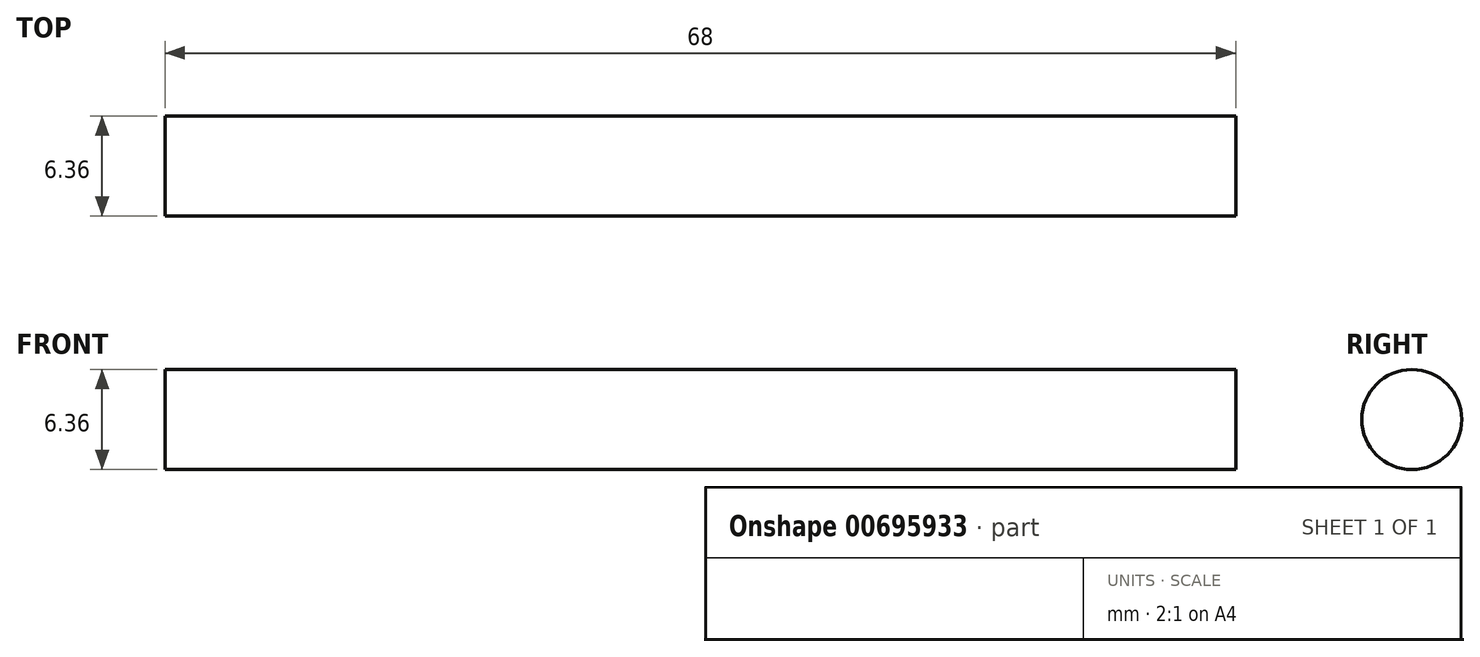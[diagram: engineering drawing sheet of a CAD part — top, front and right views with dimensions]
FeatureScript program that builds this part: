
annotation { "Feature Type Name" : "Feature", "Feature Type Description" : "" }
export const myFeature = defineFeature(function(context is Context, id is Id, definition is map)
    precondition{}
    {
        {
            var Q0;
            Q0=qCreatedBy(makeId("Right.planeOp"),FACE);
            var sketch = newSketch(context, id + "F0", { "sketchPlane" : qUnion([Q0])});
            skCircle(sketch, "E0", {"center": v(0, 0) * mm, "radius": 3.18 * mm});
            skSolve(sketch);
        }
        {
            var Q0;
            Q0 = qSketchRegion(id + "F0", true);
            extrude(context, id + "F1", {"entities" : qUnion([Q0]), "endBound" : BoundingType.SYMMETRIC, "depth" : 68 * mm, "offsetDistance" : 25 * mm});
        }
    });
